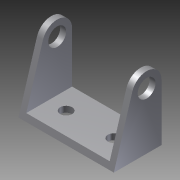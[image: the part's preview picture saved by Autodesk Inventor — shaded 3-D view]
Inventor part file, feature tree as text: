
AUTODESK INVENTOR PART (.ipt)
format: ipt  version: 2012 (Build 160160000, 160)  size: 119,808 bytes
history: native  units: in
note: dims shown in document units (in); Inventor stores cm internally (conversion verified against a paired STEP export)
features: extrude x3, sketch x3
ambient origin geometry x8: Origin, YZ Plane, XZ Plane, XY Plane, X Axis, Y Axis, Z Axis, Center Point
bodies: Solid1 (feature_tree)
feature tree (6):
  extrude  "Extrusion1"  Depth=2.0in
  extrude  "Extrusion2"  Depth=0.125in
  extrude  "Extrusion3"  Depth=1.0in TaperAngle=0.0deg
  sketch  "Sketch1"  dims[d0=1.5in d1=2.0in]
  sketch  "Sketch2"  dims[d2=0.125in d3=0.125in]
  sketch  "Sketch3"  dims[d4=0.125in d5=1.0in d6=0.0in d7=0.375in d8=1.1875in d9=0.6875in d10=1.0in d11=0.0in d12=0.25in d13=0.25in d14=0.5in d15=0.5in d16=0.5in d17=1.0in d18=0.0in]
